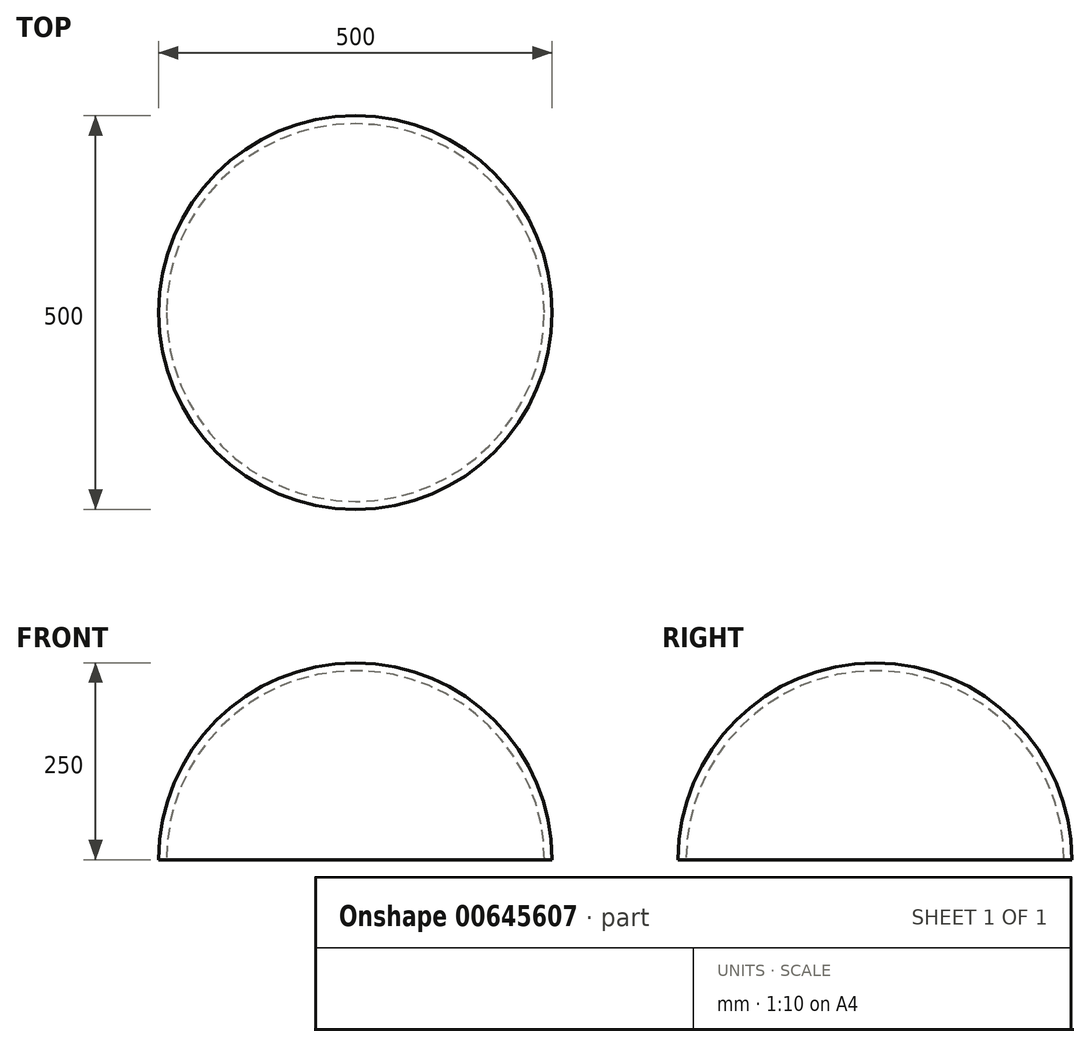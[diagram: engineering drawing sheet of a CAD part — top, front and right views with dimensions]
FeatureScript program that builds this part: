
annotation { "Feature Type Name" : "Feature", "Feature Type Description" : "" }
export const myFeature = defineFeature(function(context is Context, id is Id, definition is map)
    precondition{}
    {
        {
            var Q0;
            Q0=qCreatedBy(makeId("Top.planeOp"),FACE);
            var sketch = newSketch(context, id + "F0", { "sketchPlane" : qUnion([Q0])});
            skArc(sketch, "E0", {"start": v(240, 0) * mm, "mid": v(0, 240) * mm, "end": v(-240, 0) * mm});
            skArc(sketch, "E1", {"start": v(250, 0) * mm, "mid": v(0, 250) * mm, "end": v(-250, 0) * mm});
            skLineSegment(sketch, "E2", {"start": v(-250, 0) * mm, "end": v(-240, 0) * mm});
            skLineSegment(sketch, "E3", {"start": v(240, 0) * mm, "end": v(250, 0) * mm});
            skSolve(sketch);
        }
        {
            var Q0;
            Q0=qSketchRegion(id+"F0",true);
            var Q1;
            Q1=sQuery(id+"F0.wireOp",EDGE,"E2");
            revolve(context, id + "F1", {"entities" : qUnion([Q0]), "axis" : qUnion([Q1]), "revolveType" : RevolveType.ONE_DIRECTION, "angle" : 180 * degree});
        }
        {
            var Q0;
            Q0=qCreatedBy(makeId("Top.planeOp"),FACE);
            cPlane(context, id + "F2", {"entities" : qUnion([Q0]), "cplaneType" : CPlaneType.OFFSET, "offset" : 300 * mm, "width" : 150 * mm, "height" : 150 * mm});
        }
    });
